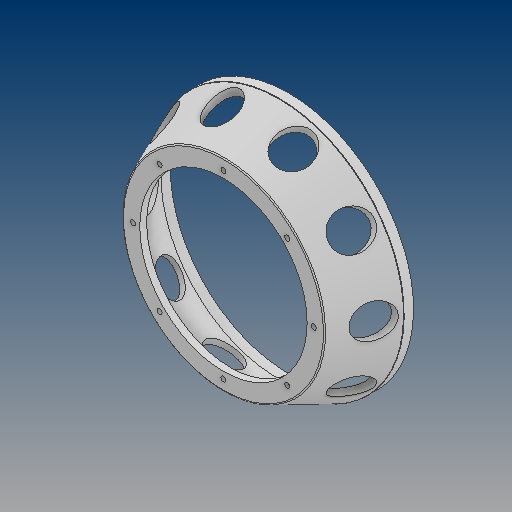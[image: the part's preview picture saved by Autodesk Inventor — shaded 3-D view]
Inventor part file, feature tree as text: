
AUTODESK INVENTOR PART (.ipt)
format: ipt  version: 2021 (Build 250183000, 183)  size: 433,664 bytes
history: native  units: in
note: dims shown in document units (in); Inventor stores cm internally (conversion verified against a paired STEP export)
features: sketch x6, revolve x3, extrude x3, pattern_circular x3, fillet x3, thread x2
ambient origin geometry x8: Origin, YZ Plane, XZ Plane, XY Plane, X Axis, Y Axis, Z Axis, Center Point
bodies: Solid2 (feature_tree)
feature tree (20):
  revolve  "Revolution1"  [1 undecoded]
  extrude  "Extrusion8"  Depth=13.5132in TaperAngle=360.0deg
  pattern_circular  "Circular Pattern9"  Count=2  [1 undecoded]
  fillet  "Fillet1"  Radius=13.5132in
  fillet  "Fillet2"  Radius=0.5511in
  fillet  "Fillet3"  Radius=13.5132in
  extrude  "Extrusion9"  Depth=0.1575in
  revolve  "Revolution3"  [1 undecoded]
  thread  "Thread27"  [1 undecoded]
  pattern_circular  "Circular Pattern10"  [2 undecoded]
  extrude  "Extrusion10"  Depth=0.3937in
  revolve  "Revolution4"  [1 undecoded]
  thread  "Thread28"  [1 undecoded]
  pattern_circular  "Circular Pattern11"  [2 undecoded]
  sketch  "Sketch1"  dims[d0=90.0deg d96=3.937in]
  sketch  "Sketch8"  dims[d97=0.0in d98=0.0in d99=3.937in d100=360.0deg d118=0.7874in d119=13.5132in d120=0.5511in d121=13.5132in]
  sketch  "Sketch9"  dims[d122=0.1575in d123=0.1575in]
  sketch  "Sketch10"  dims[d124=0.1575in d125=0.7874in d126=6.9009in]
  sketch  "Sketch11"  dims[d127=9.5762in]
  sketch  "Sketch12"  dims[d130=1.1022in d131=20.6693in d132=0.5906in d133=0.3937in d134=0.0in d137=90.0deg d138=0.2953in d139=0.0in d140=90.0deg d141=0.3937in d142=0.0in d143=3.1496in d144=360.0deg d146=0.315in d147=13.8583in d148=0.3937in d149=0.0in d150=135.0deg d151=45.0deg d152=90.0deg d153=0.3937in d154=0.0in d155=4.7244in d156=360.0deg]
note: 10 required parameter values undecoded (feature->parameter linkage not recoverable at this tier; creation-order binding heuristic only, values carry confidence <= 0.55)